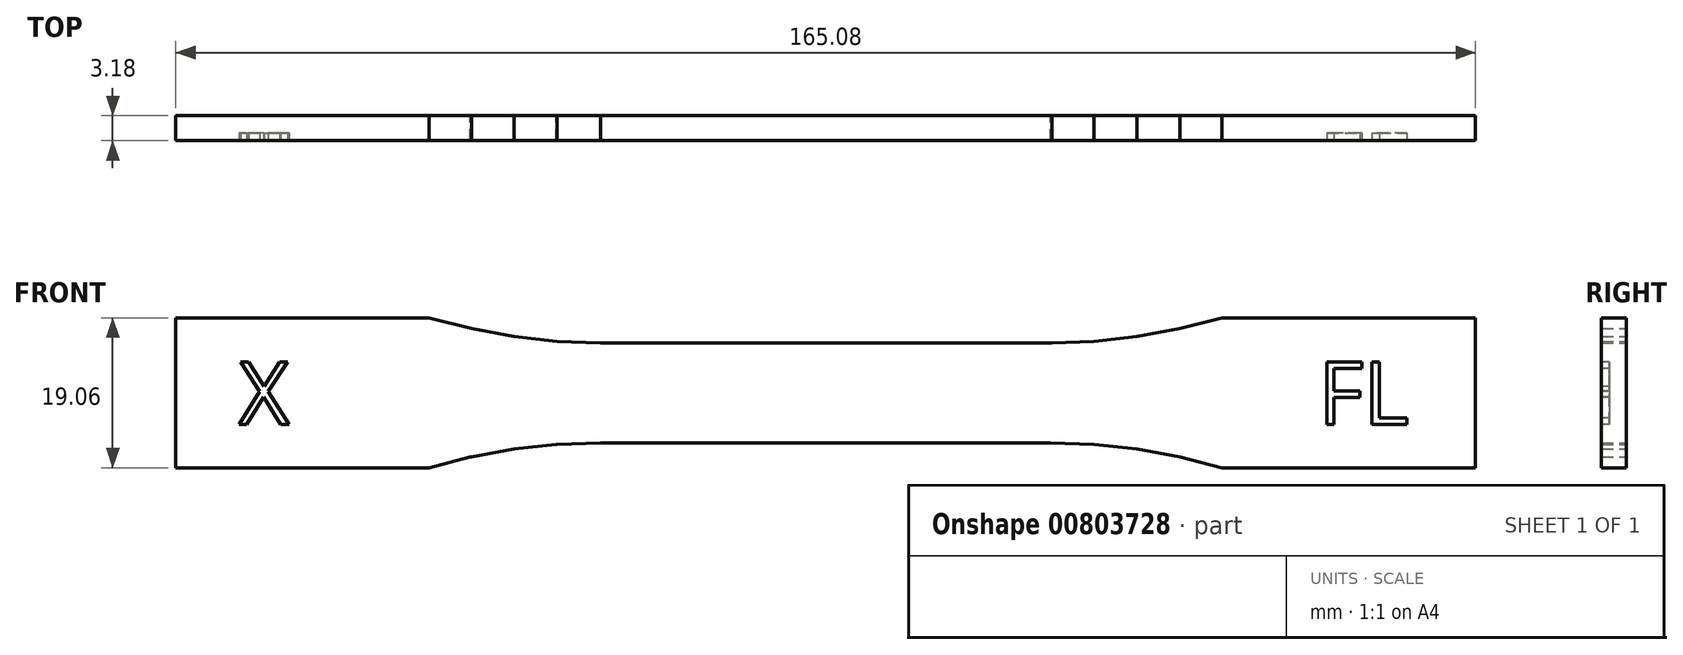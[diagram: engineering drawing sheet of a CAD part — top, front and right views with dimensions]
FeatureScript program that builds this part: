
annotation { "Feature Type Name" : "Feature", "Feature Type Description" : "" }
export const myFeature = defineFeature(function(context is Context, id is Id, definition is map)
    precondition{}
    {
        {
            var Q0;
            Q0=qCreatedBy(makeId("Front.planeOp"),FACE);
            var sketch = newSketch(context, id + "F0", { "sketchPlane" : qUnion([Q0])});
            skLineSegment(sketch, "E0", {"start": v(-45.16, -8.18) * mm, "end": v(-45, -8.13) * mm});
            skLineSegment(sketch, "E1", {"start": v(-45, -8.13) * mm, "end": v(-39.57, -7.14) * mm});
            skLineSegment(sketch, "E2", {"start": v(-39.57, -7.14) * mm, "end": v(-34.26, -6.57) * mm});
            skLineSegment(sketch, "E3", {"start": v(-34.26, -6.57) * mm, "end": v(-34.1, -6.54) * mm});
            skLineSegment(sketch, "E4", {"start": v(-34.1, -6.54) * mm, "end": v(-28.58, -6.34) * mm});
            skLineSegment(sketch, "E5", {"start": v(-28.58, -6.34) * mm, "end": v(28.58, -6.34) * mm});
            skLineSegment(sketch, "E6", {"start": v(28.58, -6.34) * mm, "end": v(34.1, -6.54) * mm});
            skLineSegment(sketch, "E7", {"start": v(34.1, -6.54) * mm, "end": v(39.57, -7.14) * mm});
            skLineSegment(sketch, "E8", {"start": v(39.57, -7.14) * mm, "end": v(45, -8.13) * mm});
            skLineSegment(sketch, "E9", {"start": v(45, -8.13) * mm, "end": v(50.34, -9.52) * mm});
            skLineSegment(sketch, "E10", {"start": v(50.34, -9.52) * mm, "end": v(82.55, -9.52) * mm});
            skLineSegment(sketch, "E11", {"start": v(82.55, -9.52) * mm, "end": v(82.55, 9.53) * mm});
            skLineSegment(sketch, "E12", {"start": v(82.55, 9.53) * mm, "end": v(50.34, 9.53) * mm});
            skLineSegment(sketch, "E13", {"start": v(50.34, 9.53) * mm, "end": v(45, 8.14) * mm});
            skLineSegment(sketch, "E14", {"start": v(45, 8.14) * mm, "end": v(39.57, 7.15) * mm});
            skLineSegment(sketch, "E15", {"start": v(39.57, 7.15) * mm, "end": v(34.1, 6.56) * mm});
            skLineSegment(sketch, "E16", {"start": v(34.1, 6.56) * mm, "end": v(28.74, 6.36) * mm});
            skLineSegment(sketch, "E17", {"start": v(28.74, 6.36) * mm, "end": v(-28.58, 6.36) * mm});
            skLineSegment(sketch, "E18", {"start": v(-28.58, 6.36) * mm, "end": v(-34.1, 6.56) * mm});
            skLineSegment(sketch, "E19", {"start": v(-34.1, 6.56) * mm, "end": v(-39.57, 7.15) * mm});
            skLineSegment(sketch, "E20", {"start": v(-39.57, 7.15) * mm, "end": v(-45, 8.14) * mm});
            skLineSegment(sketch, "E21", {"start": v(-45, 8.14) * mm, "end": v(-50.34, 9.53) * mm});
            skLineSegment(sketch, "E22", {"start": v(-50.34, 9.53) * mm, "end": v(-82.55, 9.53) * mm});
            skLineSegment(sketch, "E23", {"start": v(-82.55, 9.53) * mm, "end": v(-82.55, -9.52) * mm});
            skLineSegment(sketch, "E24", {"start": v(-82.55, -9.52) * mm, "end": v(-50.34, -9.52) * mm});
            skLineSegment(sketch, "E25", {"start": v(-50.34, -9.52) * mm, "end": v(-45.16, -8.18) * mm});
            skSolve(sketch);
        }
        {
            var Q0;
            Q0=makeQuery(id+"F0.imprint","IMPRINT",FACE,{"disambiguationData":[TD([[makeQuery(id+"F0.imprint","IMPRINT",EDGE,{"derivedFrom":sQuery(id+"F0.wireOp",EDGE,"E0")}),1.0]])]});
            extrude(context, id + "F1", {"entities" : qUnion([Q0]), "depth" : 3.18 * mm, "offsetDistance" : 25 * mm});
        }
        {
            var Q0;
            Q0=makeQuery(id+"F1.opExtrude","CAP_FACE",FACE,{"disambiguationData":[OSD([sQuery(id+"F0.wireOp",EDGE,"E0"),sQuery(id+"F0.wireOp",EDGE,"E1"),sQuery(id+"F0.wireOp",EDGE,"E2"),sQuery(id+"F0.wireOp",EDGE,"E3"),sQuery(id+"F0.wireOp",EDGE,"E4"),sQuery(id+"F0.wireOp",EDGE,"E5"),sQuery(id+"F0.wireOp",EDGE,"E6"),sQuery(id+"F0.wireOp",EDGE,"E7"),sQuery(id+"F0.wireOp",EDGE,"E8"),sQuery(id+"F0.wireOp",EDGE,"E9"),sQuery(id+"F0.wireOp",EDGE,"E10"),sQuery(id+"F0.wireOp",EDGE,"E11"),sQuery(id+"F0.wireOp",EDGE,"E12"),sQuery(id+"F0.wireOp",EDGE,"E13"),sQuery(id+"F0.wireOp",EDGE,"E14"),sQuery(id+"F0.wireOp",EDGE,"E15"),sQuery(id+"F0.wireOp",EDGE,"E16"),sQuery(id+"F0.wireOp",EDGE,"E17"),sQuery(id+"F0.wireOp",EDGE,"E18"),sQuery(id+"F0.wireOp",EDGE,"E19"),sQuery(id+"F0.wireOp",EDGE,"E20"),sQuery(id+"F0.wireOp",EDGE,"E21"),sQuery(id+"F0.wireOp",EDGE,"E22"),sQuery(id+"F0.wireOp",EDGE,"E23"),sQuery(id+"F0.wireOp",EDGE,"E24"),sQuery(id+"F0.wireOp",EDGE,"E25")])],"isStart":false});
            var sketch = newSketch(context, id + "F2", { "sketchPlane" : qUnion([Q0])});
            skText(sketch, "E26", { "text": "X", "fontName": "OpenSans-Regular.ttf"});
            skText(sketch, "E27", { "text": "FL", "fontName": "OpenSans-Regular.ttf"});
            const initialGuessF2  = {"E26": [-0.07455, -0.004, 1, 0, 0.008], "E27": [0.06258, -0.004, 1, 0, 0.008]};
            skSetInitialGuess(sketch, initialGuessF2);
            skSolve(sketch);
        }
        {
            var Q0;
            Q0 = qSketchRegion(id + "F2", true);
            extrude(context, id + "F3", {"entities" : qUnion([Q0]), "operationType" : NewBodyOperationType.REMOVE, "oppositeDirection" : true, "depth" : 1 * mm, "offsetDistance" : 25 * mm});
        }
    });
